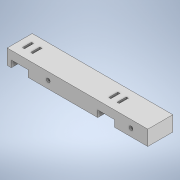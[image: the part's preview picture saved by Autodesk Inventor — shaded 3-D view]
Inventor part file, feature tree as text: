
AUTODESK INVENTOR PART (.ipt)
format: ipt  version: 2020 (Build 240168000, 168)  size: 145,920 bytes
history: native  units: mm
features: other x4, mirror x1
ambient origin geometry x8: Origin, YZ Plane, XZ Plane, XY Plane, X Axis, Y Axis, Z Axis, Center Point
bodies: Body1 (feature_tree)
feature tree (5):
  other  "side_ToF_mount_R.ipt"
  mirror  "미러1"
  other  "솔리드1::side_ToF_mount_R.ipt"
  other  "피쳐 태그1"
  other  "솔리드1"
